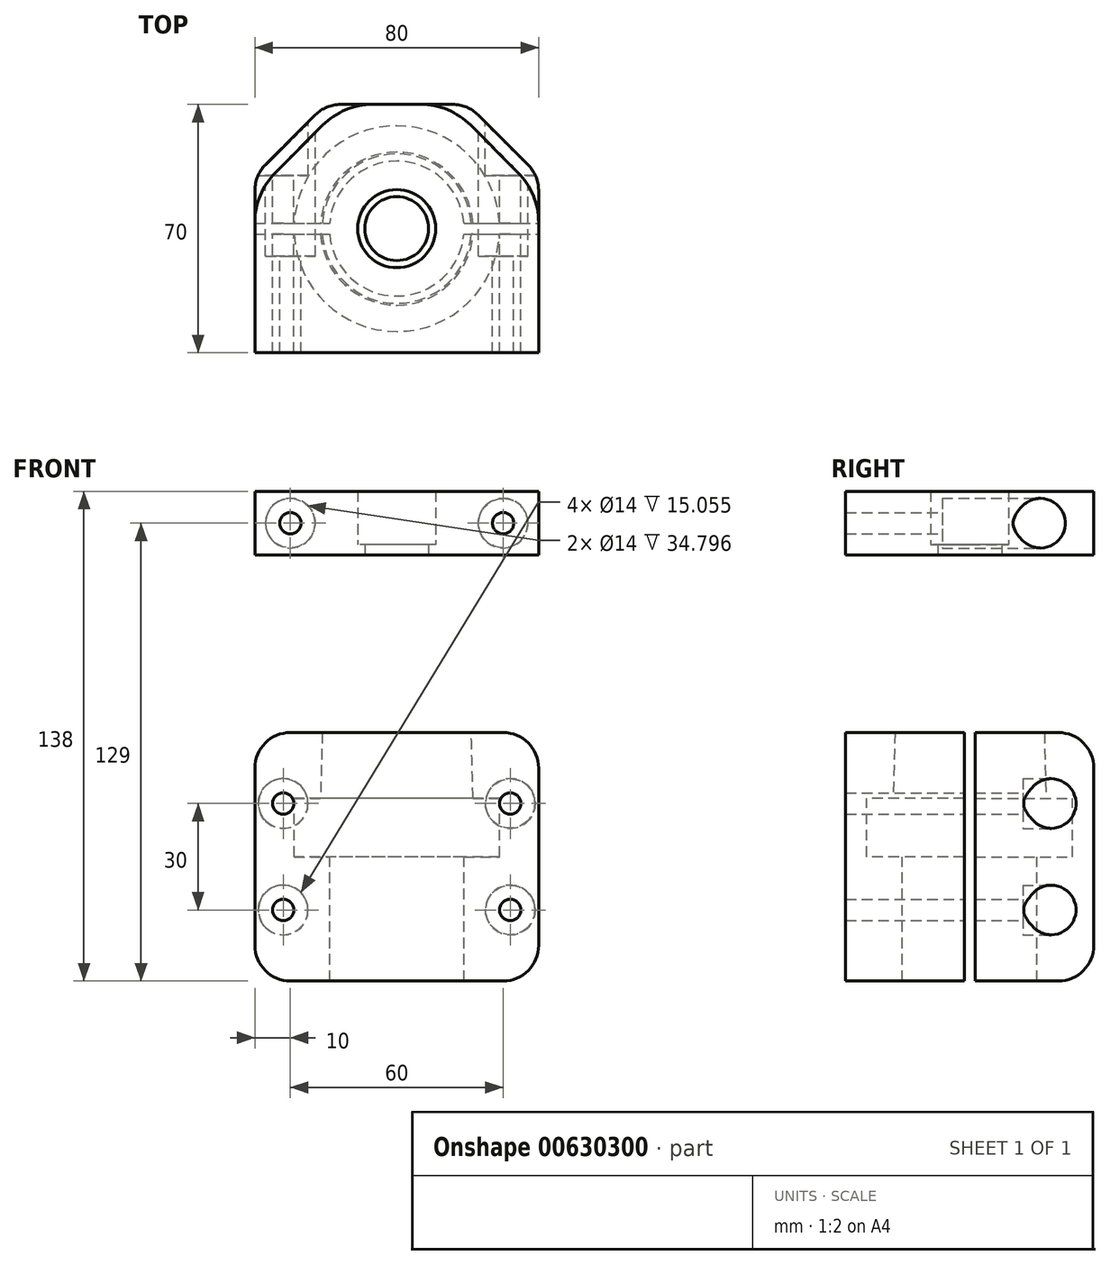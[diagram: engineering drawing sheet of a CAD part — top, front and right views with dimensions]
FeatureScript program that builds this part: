
annotation { "Feature Type Name" : "Feature", "Feature Type Description" : "" }
export const myFeature = defineFeature(function(context is Context, id is Id, definition is map)
    precondition{}
    {
        {
            var Q0;
            Q0=qCreatedBy(makeId("Front.planeOp"),FACE);
            var sketch = newSketch(context, id + "F0", { "sketchPlane" : qUnion([Q0])});
            skLineSegment(sketch, "E0", {"start": v(0, 86.22) * mm, "end": v(0, -59.94) * mm, "construction": true});
            skLineSegment(sketch, "E1.bottom", {"start": v(0, 0) * mm, "end": v(19, 0) * mm});
            skLineSegment(sketch, "E1.top", {"start": v(0, -38) * mm, "end": v(19, -38) * mm});
            skLineSegment(sketch, "E1.left", {"start": v(0, 0) * mm, "end": v(0, -38) * mm});
            skLineSegment(sketch, "E1.right", {"start": v(19, 0) * mm, "end": v(19, -38) * mm});
            skLineSegment(sketch, "E2", {"start": v(19, 0) * mm, "end": v(22, 0) * mm});
            skLineSegment(sketch, "E3", {"start": v(22, 0) * mm, "end": v(21, 36.99) * mm});
            skLineSegment(sketch, "E4", {"start": v(21, 36.99) * mm, "end": v(0, 36.99) * mm});
            skLineSegment(sketch, "E5", {"start": v(0, 36.99) * mm, "end": v(0, 0) * mm});
            skLineSegment(sketch, "E6.bottom", {"start": v(0, 0) * mm, "end": v(29, 0) * mm});
            skLineSegment(sketch, "E6.top", {"start": v(0, 16.5) * mm, "end": v(29, 16.5) * mm});
            skLineSegment(sketch, "E6.left", {"start": v(0, 0) * mm, "end": v(0, 16.5) * mm});
            skLineSegment(sketch, "E6.right", {"start": v(29, 0) * mm, "end": v(29, 16.5) * mm});
            skSolve(sketch);
        }
        {
            var Q0;
            Q0=makeQuery(id+"F0.imprint","IMPRINT",FACE,{"disambiguationData":[TD([[makeQuery(id+"F0.imprint","IMPRINT",EDGE,{"derivedFrom":sQuery(id+"F0.wireOp",EDGE,"E1.bottom")}),1.0]])]});
            var Q1;
            Q1=makeQuery(id+"F0.imprint","IMPRINT",FACE,{"disambiguationData":[TD([[makeQuery(id+"F0.imprint","IMPRINT",EDGE,{"derivedFrom":sQuery(id+"F0.wireOp",EDGE,"E1.bottom")}),-1.0]])]});
            var Q2;
            {var subQ3=sQuery(id+"F0.wireOp",EDGE,"E4");Q2=makeQuery(id+"F0.imprint","IMPRINT",FACE,{"disambiguationData":[TD([[makeQuery(id+"F0.imprint","IMPRINT",EDGE,{"derivedFrom":subQ3}),1.0]])]});}
            var Q3;
            {var subQ0=sQuery(id+"F0.wireOp",EDGE,"E6.bottom");Q3=makeQuery(id+"F0.imprint","IMPRINT",FACE,{"disambiguationData":[TD([[makeQuery(id+"F0.imprint","IMPRINT",EDGE,{"derivedFrom":subQ0}),1.0]])]});}
            var Q4;
            Q4=sQuery(id+"F0.wireOp",EDGE,"E0");
            revolve(context, id + "F1", {"surfaceOperationType" : NewSurfaceOperationType.NEW, "entities" : qUnion([Q0, Q1, Q2, Q3]), "axis" : qUnion([Q4]), "revolveType" : RevolveType.FULL});
        }
        {
            var Q0;
            Q0=qCreatedBy(makeId("Top.planeOp"),FACE);
            var sketch = newSketch(context, id + "F2", { "sketchPlane" : qUnion([Q0])});
            skLineSegment(sketch, "E7.bottom", {"start": v(-40, -35) * mm, "end": v(40, -35) * mm});
            skLineSegment(sketch, "E7.top", {"start": v(-40, 35) * mm, "end": v(40, 35) * mm});
            skLineSegment(sketch, "E7.left", {"start": v(-40, -35) * mm, "end": v(-40, 35) * mm});
            skLineSegment(sketch, "E7.right", {"start": v(40, -35) * mm, "end": v(40, 35) * mm});
            skPoint(sketch, "E7.middle", {"position": v(0, 0) * mm});
            skSolve(sketch);
        }
        {
            var Q0;
            Q0=makeQuery(id+"F2.imprint","IMPRINT",FACE,{"disambiguationData":[TD([[makeQuery(id+"F2.imprint","IMPRINT",EDGE,{"derivedFrom":sQuery(id+"F2.wireOp",EDGE,"E7.bottom")}),1.0]])]});
            extrude(context, id + "F3", {"entities" : qUnion([Q0]), "endBound" : BoundingType.SYMMETRIC, "depth" : 70 * mm, "offsetDistance" : 25 * mm});
        }
        {
            var Q0;
            Q0=makeQuery(id+"F1.opRevolve","SWEPT_BODY",BODY,{"disambiguationData":[OSD([sQuery(id+"F0.wireOp",EDGE,"E1.top"),sQuery(id+"F0.wireOp",EDGE,"E1.left"),sQuery(id+"F0.wireOp",EDGE,"E1.right"),sQuery(id+"F0.wireOp",EDGE,"E2"),sQuery(id+"F0.wireOp",EDGE,"E3"),sQuery(id+"F0.wireOp",EDGE,"E4"),sQuery(id+"F0.wireOp",EDGE,"E5")])]});
            var Q1;
            Q1=makeQuery(id+"F3.opExtrude","SWEPT_BODY",BODY,{"disambiguationData":[OSD([sQuery(id+"F2.wireOp",EDGE,"E7.bottom"),sQuery(id+"F2.wireOp",EDGE,"E7.top"),sQuery(id+"F2.wireOp",EDGE,"E7.left"),sQuery(id+"F2.wireOp",EDGE,"E7.right")])]});
            booleanBodies(context, id + "F4", {"operationType" : BooleanOperationType.SUBTRACTION, "tools" : qUnion([Q0]), "targets" : qUnion([Q1])});
        }
        {
            var Q0;
            Q0=makeQuery(id+"F3.opExtrude","CAP_FACE",FACE,{"disambiguationData":[OSD([sQuery(id+"F2.wireOp",EDGE,"E7.bottom"),sQuery(id+"F2.wireOp",EDGE,"E7.top"),sQuery(id+"F2.wireOp",EDGE,"E7.left"),sQuery(id+"F2.wireOp",EDGE,"E7.right")])],"isStart":true});
            var sketch = newSketch(context, id + "F5", { "sketchPlane" : qUnion([Q0])});
            skLineSegment(sketch, "E8.bottom", {"start": v(-40, 1.5) * mm, "end": v(40, 1.5) * mm});
            skLineSegment(sketch, "E8.top", {"start": v(-40, -1.5) * mm, "end": v(40, -1.5) * mm});
            skLineSegment(sketch, "E8.left", {"start": v(-40, 1.5) * mm, "end": v(-40, -1.5) * mm});
            skLineSegment(sketch, "E8.right", {"start": v(40, 1.5) * mm, "end": v(40, -1.5) * mm});
            skPoint(sketch, "E8.middle", {"position": v(0, 0) * mm});
            skSolve(sketch);
        }
        {
            var Q0;
            Q0 = qSketchRegion(id + "F5", true);
            extrude(context, id + "F6", {"entities" : qUnion([Q0]), "endBound" : BoundingType.SYMMETRIC, "depth" : 200 * mm, "offsetDistance" : 25 * mm});
        }
        {
            var Q0;
            Q0=makeQuery(id+"F6.opExtrude","SWEPT_BODY",BODY,{"disambiguationData":[OSD([sQuery(id+"F5.wireOp",EDGE,"E8.bottom"),sQuery(id+"F5.wireOp",EDGE,"E8.top"),sQuery(id+"F5.wireOp",EDGE,"E8.left"),sQuery(id+"F5.wireOp",EDGE,"E8.right")])]});
            var Q1;
            Q1=makeQuery(id+"F3.opExtrude","SWEPT_BODY",BODY,{"disambiguationData":[OSD([sQuery(id+"F2.wireOp",EDGE,"E7.bottom"),sQuery(id+"F2.wireOp",EDGE,"E7.top"),sQuery(id+"F2.wireOp",EDGE,"E7.left"),sQuery(id+"F2.wireOp",EDGE,"E7.right")])]});
            booleanBodies(context, id + "F7", {"operationType" : BooleanOperationType.SUBTRACTION, "tools" : qUnion([Q0]), "targets" : qUnion([Q1])});
        }
        {
            var Q0;
            Q0=makeQuery(id+"F3.opExtrude","SWEPT_FACE",FACE,{"disambiguationData":[OSD([sQuery(id+"F2.wireOp",EDGE,"E7.top")])]});
            var sketch = newSketch(context, id + "F8", { "sketchPlane" : qUnion([Q0])});
            skLineSegment(sketch, "E9", {"start": v(32, 0) * mm, "end": v(32, -15) * mm, "construction": true});
            skLineSegment(sketch, "E10", {"start": v(32, 0) * mm, "end": v(32, 15) * mm, "construction": true});
            skLineSegment(sketch, "E11", {"start": v(-32, 0) * mm, "end": v(-32, -15) * mm, "construction": true});
            skLineSegment(sketch, "E12", {"start": v(-32, 0) * mm, "end": v(-32, 15) * mm, "construction": true});
            skSolve(sketch);
        }
        {
            var Q0;
            Q0=sQuery(id+"F8.wireOp",VERTEX,"E9.end");
            var Q1;
            Q1=sQuery(id+"F8.wireOp",VERTEX,"E10.end");
            var Q2;
            Q2=sQuery(id+"F8.wireOp",VERTEX,"E12.end");
            var Q3;
            Q3=sQuery(id+"F8.wireOp",VERTEX,"E11.end");
            var Q4;
            Q4=makeQuery(id+"F7.opBoolean","SPLIT",BODY,{"disambiguationData":[OD(0.0)],"derivedFrom":makeQuery(id+"F3.opExtrude","SWEPT_BODY",BODY,{"disambiguationData":[OSD([sQuery(id+"F2.wireOp",EDGE,"E7.bottom"),sQuery(id+"F2.wireOp",EDGE,"E7.top"),sQuery(id+"F2.wireOp",EDGE,"E7.left"),sQuery(id+"F2.wireOp",EDGE,"E7.right")])]})});
            var Q5;
            Q5=makeQuery(id+"F7.opBoolean","SPLIT",BODY,{"disambiguationData":[OD(1.0)],"derivedFrom":makeQuery(id+"F3.opExtrude","SWEPT_BODY",BODY,{"disambiguationData":[OSD([sQuery(id+"F2.wireOp",EDGE,"E7.bottom"),sQuery(id+"F2.wireOp",EDGE,"E7.top"),sQuery(id+"F2.wireOp",EDGE,"E7.left"),sQuery(id+"F2.wireOp",EDGE,"E7.right")])]})});
            hole(context, id + "F9", {"style" : HoleStyle.C_BORE, "endStyle" : HoleEndStyle.THROUGH, "holeDiameter" : 6 * mm, "cBoreDiameter" : 14 * mm, "cBoreDepth" : 20 * mm, "majorDiameter" : 5 * mm, "isTappedThrough" : true, "tappedDepth" : 12 * mm, "tapClearance" : 3, "startFromSketch" : true, "locations" : qUnion([Q0, Q1, Q2, Q3]), "scope" : qUnion([Q4, Q5])});
        }
        {
            var Q0;
            Q0=makeQuery(id+"F3.opExtrude","SWEPT_EDGE",EDGE,{"disambiguationData":[OSD([sQuery(id+"F2.wireOp",EDGE,"E7.top"),sQuery(id+"F2.wireOp",EDGE,"E7.right")])]});
            var Q1;
            Q1=makeQuery(id+"F3.opExtrude","SWEPT_EDGE",EDGE,{"disambiguationData":[OSD([sQuery(id+"F2.wireOp",EDGE,"E7.top"),sQuery(id+"F2.wireOp",EDGE,"E7.left")])]});
            chamfer(context, id + "F10", {"entities" : qUnion([Q0, Q1]), "width" : 20 * mm, "tangentPropagation" : true});
        }
        {
            var Q0;
            {var subQ0=sQuery(id+"F2.wireOp",EDGE,"E7.bottom");var subQ1=sQuery(id+"F2.wireOp",EDGE,"E7.left");Q0=makeQuery(id+"F7.opBoolean","SPLIT",EDGE,{"disambiguationData":[TD([makeQuery(id+"F3.opExtrude","SWEPT_FACE",FACE,{"disambiguationData":[OSD([subQ0])]})])],"derivedFrom":makeQuery(id+"F3.opExtrude","CAP_EDGE",EDGE,{"disambiguationData":[OSD([subQ1])],"isStart":false})});}
            var Q1;
            {var subQ0=sQuery(id+"F2.wireOp",EDGE,"E7.left");var subQ1=sQuery(id+"F2.wireOp",EDGE,"E7.top");Q1=makeQuery(id+"F7.opBoolean","SPLIT",EDGE,{"disambiguationData":[TD([makeQuery(id+"F3.opExtrude","SWEPT_FACE",FACE,{"disambiguationData":[OSD([subQ1])]})])],"derivedFrom":makeQuery(id+"F3.opExtrude","CAP_EDGE",EDGE,{"disambiguationData":[OSD([subQ0])],"isStart":false})});}
            var Q2;
            {var subQ0=sQuery(id+"F2.wireOp",EDGE,"E7.right");var subQ1=sQuery(id+"F2.wireOp",EDGE,"E7.left");var subQ2=sQuery(id+"F2.wireOp",EDGE,"E7.top");Q2=makeQuery(id+"F10.opChamfer","BLEND_EDGE",EDGE,{"blendedFrom":[makeQuery(id+"F3.opExtrude","SWEPT_EDGE",EDGE,{"disambiguationData":[OSD([subQ2,subQ1])]}),makeQuery(id+"F7.opBoolean","SPLIT",FACE,{"disambiguationData":[TD([makeQuery(id+"F3.opExtrude","SWEPT_FACE",FACE,{"disambiguationData":[OSD([subQ2])]})])],"derivedFrom":makeQuery(id+"F3.opExtrude","CAP_FACE",FACE,{"disambiguationData":[OSD([sQuery(id+"F2.wireOp",EDGE,"E7.bottom"),subQ2,subQ1,subQ0])],"isStart":false})})],"blendedInto":[makeQuery(id+"F7.opBoolean","SPLIT",FACE,{"disambiguationData":[TD([makeQuery(id+"F3.opExtrude","SWEPT_FACE",FACE,{"disambiguationData":[OSD([subQ2])]})])],"derivedFrom":makeQuery(id+"F3.opExtrude","CAP_FACE",FACE,{"disambiguationData":[OSD([sQuery(id+"F2.wireOp",EDGE,"E7.bottom"),subQ2,subQ1,subQ0])],"isStart":false})})]});}
            var Q3;
            Q3=makeQuery(id+"F3.opExtrude","CAP_EDGE",EDGE,{"disambiguationData":[OSD([sQuery(id+"F2.wireOp",EDGE,"E7.top")])],"isStart":false});
            var Q4;
            {var subQ0=sQuery(id+"F2.wireOp",EDGE,"E7.right");var subQ1=sQuery(id+"F2.wireOp",EDGE,"E7.left");var subQ2=sQuery(id+"F2.wireOp",EDGE,"E7.top");Q4=makeQuery(id+"F10.opChamfer","BLEND_EDGE",EDGE,{"blendedFrom":[makeQuery(id+"F3.opExtrude","SWEPT_EDGE",EDGE,{"disambiguationData":[OSD([subQ2,subQ0])]}),makeQuery(id+"F7.opBoolean","SPLIT",FACE,{"disambiguationData":[TD([makeQuery(id+"F3.opExtrude","SWEPT_FACE",FACE,{"disambiguationData":[OSD([subQ2])]})])],"derivedFrom":makeQuery(id+"F3.opExtrude","CAP_FACE",FACE,{"disambiguationData":[OSD([sQuery(id+"F2.wireOp",EDGE,"E7.bottom"),subQ2,subQ1,subQ0])],"isStart":false})})],"blendedInto":[makeQuery(id+"F7.opBoolean","SPLIT",FACE,{"disambiguationData":[TD([makeQuery(id+"F3.opExtrude","SWEPT_FACE",FACE,{"disambiguationData":[OSD([subQ2])]})])],"derivedFrom":makeQuery(id+"F3.opExtrude","CAP_FACE",FACE,{"disambiguationData":[OSD([sQuery(id+"F2.wireOp",EDGE,"E7.bottom"),subQ2,subQ1,subQ0])],"isStart":false})})]});}
            var Q5;
            {var subQ0=sQuery(id+"F2.wireOp",EDGE,"E7.right");var subQ1=sQuery(id+"F2.wireOp",EDGE,"E7.top");Q5=makeQuery(id+"F7.opBoolean","SPLIT",EDGE,{"disambiguationData":[TD([makeQuery(id+"F3.opExtrude","SWEPT_FACE",FACE,{"disambiguationData":[OSD([subQ1])]})])],"derivedFrom":makeQuery(id+"F3.opExtrude","CAP_EDGE",EDGE,{"disambiguationData":[OSD([subQ0])],"isStart":false})});}
            var Q6;
            {var subQ0=sQuery(id+"F2.wireOp",EDGE,"E7.bottom");var subQ1=sQuery(id+"F2.wireOp",EDGE,"E7.right");Q6=makeQuery(id+"F7.opBoolean","SPLIT",EDGE,{"disambiguationData":[TD([makeQuery(id+"F3.opExtrude","SWEPT_FACE",FACE,{"disambiguationData":[OSD([subQ0])]})])],"derivedFrom":makeQuery(id+"F3.opExtrude","CAP_EDGE",EDGE,{"disambiguationData":[OSD([subQ1])],"isStart":false})});}
            var Q7;
            {var subQ0=sQuery(id+"F2.wireOp",EDGE,"E7.bottom");var subQ1=sQuery(id+"F2.wireOp",EDGE,"E7.right");Q7=makeQuery(id+"F7.opBoolean","SPLIT",EDGE,{"disambiguationData":[TD([makeQuery(id+"F3.opExtrude","SWEPT_FACE",FACE,{"disambiguationData":[OSD([subQ0])]})])],"derivedFrom":makeQuery(id+"F3.opExtrude","CAP_EDGE",EDGE,{"disambiguationData":[OSD([subQ1])],"isStart":true})});}
            var Q8;
            {var subQ0=sQuery(id+"F2.wireOp",EDGE,"E7.right");var subQ1=sQuery(id+"F2.wireOp",EDGE,"E7.top");Q8=makeQuery(id+"F7.opBoolean","SPLIT",EDGE,{"disambiguationData":[TD([makeQuery(id+"F3.opExtrude","SWEPT_FACE",FACE,{"disambiguationData":[OSD([subQ1])]})])],"derivedFrom":makeQuery(id+"F3.opExtrude","CAP_EDGE",EDGE,{"disambiguationData":[OSD([subQ0])],"isStart":true})});}
            var Q9;
            {var subQ0=sQuery(id+"F2.wireOp",EDGE,"E7.left");var subQ1=sQuery(id+"F2.wireOp",EDGE,"E7.right");var subQ2=sQuery(id+"F2.wireOp",EDGE,"E7.top");Q9=makeQuery(id+"F10.opChamfer","BLEND_EDGE",EDGE,{"blendedFrom":[makeQuery(id+"F3.opExtrude","SWEPT_EDGE",EDGE,{"disambiguationData":[OSD([subQ2,subQ1])]}),makeQuery(id+"F7.opBoolean","SPLIT",FACE,{"disambiguationData":[TD([makeQuery(id+"F3.opExtrude","SWEPT_FACE",FACE,{"disambiguationData":[OSD([subQ2])]})])],"derivedFrom":makeQuery(id+"F3.opExtrude","CAP_FACE",FACE,{"disambiguationData":[OSD([sQuery(id+"F2.wireOp",EDGE,"E7.bottom"),subQ2,subQ0,subQ1])],"isStart":true})})],"blendedInto":[makeQuery(id+"F7.opBoolean","SPLIT",FACE,{"disambiguationData":[TD([makeQuery(id+"F3.opExtrude","SWEPT_FACE",FACE,{"disambiguationData":[OSD([subQ2])]})])],"derivedFrom":makeQuery(id+"F3.opExtrude","CAP_FACE",FACE,{"disambiguationData":[OSD([sQuery(id+"F2.wireOp",EDGE,"E7.bottom"),subQ2,subQ0,subQ1])],"isStart":true})})]});}
            var Q10;
            Q10=makeQuery(id+"F3.opExtrude","CAP_EDGE",EDGE,{"disambiguationData":[OSD([sQuery(id+"F2.wireOp",EDGE,"E7.top")])],"isStart":true});
            var Q11;
            {var subQ0=sQuery(id+"F2.wireOp",EDGE,"E7.left");var subQ1=sQuery(id+"F2.wireOp",EDGE,"E7.right");var subQ2=sQuery(id+"F2.wireOp",EDGE,"E7.top");Q11=makeQuery(id+"F10.opChamfer","BLEND_EDGE",EDGE,{"blendedFrom":[makeQuery(id+"F3.opExtrude","SWEPT_EDGE",EDGE,{"disambiguationData":[OSD([subQ2,subQ0])]}),makeQuery(id+"F7.opBoolean","SPLIT",FACE,{"disambiguationData":[TD([makeQuery(id+"F3.opExtrude","SWEPT_FACE",FACE,{"disambiguationData":[OSD([subQ2])]})])],"derivedFrom":makeQuery(id+"F3.opExtrude","CAP_FACE",FACE,{"disambiguationData":[OSD([sQuery(id+"F2.wireOp",EDGE,"E7.bottom"),subQ2,subQ0,subQ1])],"isStart":true})})],"blendedInto":[makeQuery(id+"F7.opBoolean","SPLIT",FACE,{"disambiguationData":[TD([makeQuery(id+"F3.opExtrude","SWEPT_FACE",FACE,{"disambiguationData":[OSD([subQ2])]})])],"derivedFrom":makeQuery(id+"F3.opExtrude","CAP_FACE",FACE,{"disambiguationData":[OSD([sQuery(id+"F2.wireOp",EDGE,"E7.bottom"),subQ2,subQ0,subQ1])],"isStart":true})})]});}
            var Q12;
            {var subQ0=sQuery(id+"F2.wireOp",EDGE,"E7.left");var subQ1=sQuery(id+"F2.wireOp",EDGE,"E7.top");Q12=makeQuery(id+"F7.opBoolean","SPLIT",EDGE,{"disambiguationData":[TD([makeQuery(id+"F3.opExtrude","SWEPT_FACE",FACE,{"disambiguationData":[OSD([subQ1])]})])],"derivedFrom":makeQuery(id+"F3.opExtrude","CAP_EDGE",EDGE,{"disambiguationData":[OSD([subQ0])],"isStart":true})});}
            var Q13;
            {var subQ0=sQuery(id+"F2.wireOp",EDGE,"E7.bottom");var subQ1=sQuery(id+"F2.wireOp",EDGE,"E7.left");Q13=makeQuery(id+"F7.opBoolean","SPLIT",EDGE,{"disambiguationData":[TD([makeQuery(id+"F3.opExtrude","SWEPT_FACE",FACE,{"disambiguationData":[OSD([subQ0])]})])],"derivedFrom":makeQuery(id+"F3.opExtrude","CAP_EDGE",EDGE,{"disambiguationData":[OSD([subQ1])],"isStart":true})});}
            var Q14;
            {var subQ0=sQuery(id+"F2.wireOp",EDGE,"E7.right");var subQ2=sQuery(id+"F2.wireOp",EDGE,"E7.top");Q14=makeQuery(id+"F10.opChamfer","BLEND_EDGE",EDGE,{"blendedFrom":[makeQuery(id+"F3.opExtrude","SWEPT_EDGE",EDGE,{"disambiguationData":[OSD([subQ2,subQ0])]}),makeQuery(id+"F7.opBoolean","SPLIT",FACE,{"disambiguationData":[TD([makeQuery(id+"F3.opExtrude","SWEPT_FACE",FACE,{"disambiguationData":[OSD([subQ2])]})])],"derivedFrom":makeQuery(id+"F3.opExtrude","SWEPT_FACE",FACE,{"disambiguationData":[OSD([subQ0])]})})],"blendedInto":[makeQuery(id+"F7.opBoolean","SPLIT",FACE,{"disambiguationData":[TD([makeQuery(id+"F3.opExtrude","SWEPT_FACE",FACE,{"disambiguationData":[OSD([subQ2])]})])],"derivedFrom":makeQuery(id+"F3.opExtrude","SWEPT_FACE",FACE,{"disambiguationData":[OSD([subQ0])]})})]});}
            var Q15;
            {var subQ0=sQuery(id+"F2.wireOp",EDGE,"E7.top");Q15=makeQuery(id+"F10.opChamfer","BLEND_EDGE",EDGE,{"blendedFrom":[makeQuery(id+"F3.opExtrude","SWEPT_EDGE",EDGE,{"disambiguationData":[OSD([subQ0,sQuery(id+"F2.wireOp",EDGE,"E7.right")])]}),makeQuery(id+"F3.opExtrude","SWEPT_FACE",FACE,{"disambiguationData":[OSD([subQ0])]})],"blendedInto":[makeQuery(id+"F3.opExtrude","SWEPT_FACE",FACE,{"disambiguationData":[OSD([subQ0])]})]});}
            var Q16;
            {var subQ0=sQuery(id+"F2.wireOp",EDGE,"E7.top");Q16=makeQuery(id+"F10.opChamfer","BLEND_EDGE",EDGE,{"blendedFrom":[makeQuery(id+"F3.opExtrude","SWEPT_EDGE",EDGE,{"disambiguationData":[OSD([subQ0,sQuery(id+"F2.wireOp",EDGE,"E7.left")])]}),makeQuery(id+"F3.opExtrude","SWEPT_FACE",FACE,{"disambiguationData":[OSD([subQ0])]})],"blendedInto":[makeQuery(id+"F3.opExtrude","SWEPT_FACE",FACE,{"disambiguationData":[OSD([subQ0])]})]});}
            var Q17;
            {var subQ1=sQuery(id+"F2.wireOp",EDGE,"E7.left");var subQ2=sQuery(id+"F2.wireOp",EDGE,"E7.top");Q17=makeQuery(id+"F10.opChamfer","BLEND_EDGE",EDGE,{"blendedFrom":[makeQuery(id+"F3.opExtrude","SWEPT_EDGE",EDGE,{"disambiguationData":[OSD([subQ2,subQ1])]}),makeQuery(id+"F7.opBoolean","SPLIT",FACE,{"disambiguationData":[TD([makeQuery(id+"F3.opExtrude","SWEPT_FACE",FACE,{"disambiguationData":[OSD([subQ2])]})])],"derivedFrom":makeQuery(id+"F3.opExtrude","SWEPT_FACE",FACE,{"disambiguationData":[OSD([subQ1])]})})],"blendedInto":[makeQuery(id+"F7.opBoolean","SPLIT",FACE,{"disambiguationData":[TD([makeQuery(id+"F3.opExtrude","SWEPT_FACE",FACE,{"disambiguationData":[OSD([subQ2])]})])],"derivedFrom":makeQuery(id+"F3.opExtrude","SWEPT_FACE",FACE,{"disambiguationData":[OSD([subQ1])]})})]});}
            fillet(context, id + "F11", {"entities" : qUnion([Q0, Q1, Q2, Q3, Q4, Q5, Q6, Q7, Q8, Q9, Q10, Q11, Q12, Q13, Q14, Q15, Q16, Q17]), "tangentPropagation" : true, "radius" : 10 * mm, "defaultsChanged" : true, "vertexSettings" : [], "allowEdgeOverflow" : false});
        }
        {
            var Q0;
            {var subQ0=sQuery(id+"F2.wireOp",EDGE,"E7.left");var subQ1=sQuery(id+"F2.wireOp",EDGE,"E7.right");var subQ2=sQuery(id+"F2.wireOp",EDGE,"E7.bottom");Q0=makeQuery(id+"F7.opBoolean","SPLIT",FACE,{"disambiguationData":[TD([makeQuery(id+"F3.opExtrude","SWEPT_FACE",FACE,{"disambiguationData":[OSD([subQ2])]})])],"derivedFrom":makeQuery(id+"F3.opExtrude","CAP_FACE",FACE,{"disambiguationData":[OSD([subQ2,sQuery(id+"F2.wireOp",EDGE,"E7.top"),subQ0,subQ1])],"isStart":false})});}
            cPlane(context, id + "F12", {"entities" : qUnion([Q0]), "cplaneType" : CPlaneType.OFFSET, "offset" : 50 * mm, "width" : 150 * mm, "height" : 150 * mm});
        }
        {
            var Q0;
            Q0=qCreatedBy(id+"F12.planeOp",FACE);
            var sketch = newSketch(context, id + "F13", { "sketchPlane" : qUnion([Q0])});
            skPoint(sketch, "E13.0", {"position": v(0, 0) * mm});
            skLineSegment(sketch, "E14.0", {"start": v(-30, -35) * mm, "end": v(30, -35) * mm});
            skLineSegment(sketch, "E15.0", {"start": v(-15.86, 35) * mm, "end": v(15.86, 35) * mm});
            skLineSegment(sketch, "E16.0", {"start": v(-40, -35) * mm, "end": v(-40, -1.5) * mm});
            skLineSegment(sketch, "E17.0", {"start": v(40, -1.5) * mm, "end": v(40, -35) * mm});
            skLineSegment(sketch, "E18", {"start": v(40, -35) * mm, "end": v(30, -35) * mm});
            skLineSegment(sketch, "E19", {"start": v(-30, -35) * mm, "end": v(-40, -35) * mm});
            skCircle(sketch, "E20", {"center": v(0, 0) * mm, "radius": 9 * mm});
            skCircle(sketch, "E21", {"center": v(0, 0) * mm, "radius": 11 * mm});
            skLineSegment(sketch, "E22", {"start": v(40, -1.5) * mm, "end": v(40, 35) * mm});
            skLineSegment(sketch, "E23", {"start": v(40, 35) * mm, "end": v(15.86, 35) * mm});
            skLineSegment(sketch, "E24", {"start": v(-40, -1.5) * mm, "end": v(-40, 35) * mm});
            skLineSegment(sketch, "E25", {"start": v(-40, 35) * mm, "end": v(-15.86, 35) * mm});
            skSolve(sketch);
        }
        {
            var Q0;
            Q0=makeQuery(id+"F13.imprint","IMPRINT",FACE,{"disambiguationData":[TD([[makeQuery(id+"F13.imprint","IMPRINT",EDGE,{"derivedFrom":sQuery(id+"F13.wireOp",EDGE,"E14.0")}),1.0]])]});
            extrude(context, id + "F14", {"entities" : qUnion([Q0]), "depth" : 18 * mm, "offsetDistance" : 25 * mm});
        }
        {
            var Q0;
            Q0=makeQuery(id+"F14.opExtrude","SWEPT_FACE",FACE,{"disambiguationData":[OSD([sQuery(id+"F13.wireOp",EDGE,"E15.0"),sQuery(id+"F13.wireOp",EDGE,"E23"),sQuery(id+"F13.wireOp",EDGE,"E25")])]});
            var sketch = newSketch(context, id + "F15", { "sketchPlane" : qUnion([Q0])});
            skLineSegment(sketch, "E26", {"start": v(40, 94) * mm, "end": v(30, 94) * mm, "construction": true});
            skLineSegment(sketch, "E27", {"start": v(-40, 94) * mm, "end": v(-30, 94) * mm, "construction": true});
            skSolve(sketch);
        }
        {
            var Q0;
            Q0=makeQuery(id+"F13.imprint","IMPRINT",FACE,{"disambiguationData":[TD([[makeQuery(id+"F13.imprint","IMPRINT",EDGE,{"derivedFrom":sQuery(id+"F13.wireOp",EDGE,"E20")}),-1.0]])]});
            extrude(context, id + "F16", {"entities" : qUnion([Q0]), "operationType" : NewBodyOperationType.ADD, "depth" : 3 * mm, "offsetDistance" : 25 * mm});
        }
        {
            var Q0;
            Q0=makeQuery(id+"F14.opExtrude","SWEPT_EDGE",EDGE,{"disambiguationData":[OSD([sQuery(id+"F13.wireOp",EDGE,"E22"),sQuery(id+"F13.wireOp",EDGE,"E23")])]});
            var Q1;
            Q1=makeQuery(id+"F14.opExtrude","SWEPT_EDGE",EDGE,{"disambiguationData":[OSD([sQuery(id+"F13.wireOp",EDGE,"E24"),sQuery(id+"F13.wireOp",EDGE,"E25")])]});
            chamfer(context, id + "F17", {"entities" : qUnion([Q0, Q1]), "width" : 25 * mm, "tangentPropagation" : true});
        }
        {
            var Q0;
            {var subQ0=sQuery(id+"F13.wireOp",EDGE,"E23");Q0=makeQuery(id+"F17.opChamfer","BLEND_EDGE",EDGE,{"blendedFrom":[makeQuery(id+"F14.opExtrude","SWEPT_EDGE",EDGE,{"disambiguationData":[OSD([sQuery(id+"F13.wireOp",EDGE,"E22"),subQ0])]}),makeQuery(id+"F14.opExtrude","SWEPT_FACE",FACE,{"disambiguationData":[OSD([sQuery(id+"F13.wireOp",EDGE,"E15.0"),subQ0,sQuery(id+"F13.wireOp",EDGE,"E25")])]})],"blendedInto":[makeQuery(id+"F14.opExtrude","SWEPT_FACE",FACE,{"disambiguationData":[OSD([sQuery(id+"F13.wireOp",EDGE,"E15.0"),subQ0,sQuery(id+"F13.wireOp",EDGE,"E25")])]})]});}
            var Q1;
            {var subQ0=sQuery(id+"F13.wireOp",EDGE,"E22");Q1=makeQuery(id+"F17.opChamfer","BLEND_EDGE",EDGE,{"blendedFrom":[makeQuery(id+"F14.opExtrude","SWEPT_EDGE",EDGE,{"disambiguationData":[OSD([subQ0,sQuery(id+"F13.wireOp",EDGE,"E23")])]}),makeQuery(id+"F14.opExtrude","SWEPT_FACE",FACE,{"disambiguationData":[OSD([sQuery(id+"F13.wireOp",EDGE,"E17.0"),subQ0])]})],"blendedInto":[makeQuery(id+"F14.opExtrude","SWEPT_FACE",FACE,{"disambiguationData":[OSD([sQuery(id+"F13.wireOp",EDGE,"E17.0"),subQ0])]})]});}
            var Q2;
            {var subQ0=sQuery(id+"F13.wireOp",EDGE,"E25");Q2=makeQuery(id+"F17.opChamfer","BLEND_EDGE",EDGE,{"blendedFrom":[makeQuery(id+"F14.opExtrude","SWEPT_EDGE",EDGE,{"disambiguationData":[OSD([sQuery(id+"F13.wireOp",EDGE,"E24"),subQ0])]}),makeQuery(id+"F14.opExtrude","SWEPT_FACE",FACE,{"disambiguationData":[OSD([sQuery(id+"F13.wireOp",EDGE,"E15.0"),sQuery(id+"F13.wireOp",EDGE,"E23"),subQ0])]})],"blendedInto":[makeQuery(id+"F14.opExtrude","SWEPT_FACE",FACE,{"disambiguationData":[OSD([sQuery(id+"F13.wireOp",EDGE,"E15.0"),sQuery(id+"F13.wireOp",EDGE,"E23"),subQ0])]})]});}
            var Q3;
            {var subQ0=sQuery(id+"F13.wireOp",EDGE,"E24");Q3=makeQuery(id+"F17.opChamfer","BLEND_EDGE",EDGE,{"blendedFrom":[makeQuery(id+"F14.opExtrude","SWEPT_EDGE",EDGE,{"disambiguationData":[OSD([subQ0,sQuery(id+"F13.wireOp",EDGE,"E25")])]}),makeQuery(id+"F14.opExtrude","SWEPT_FACE",FACE,{"disambiguationData":[OSD([sQuery(id+"F13.wireOp",EDGE,"E16.0"),subQ0])]})],"blendedInto":[makeQuery(id+"F14.opExtrude","SWEPT_FACE",FACE,{"disambiguationData":[OSD([sQuery(id+"F13.wireOp",EDGE,"E16.0"),subQ0])]})]});}
            fillet(context, id + "F18", {"entities" : qUnion([Q0, Q1, Q2, Q3]), "tangentPropagation" : true, "radius" : 20 * mm, "defaultsChanged" : true, "vertexSettings" : [], "allowEdgeOverflow" : false});
        }
        {
            var Q0;
            Q0=sQuery(id+"F15.wireOp",VERTEX,"E26.end");
            var Q1;
            Q1=sQuery(id+"F15.wireOp",VERTEX,"E27.end");
            var Q2;
            Q2=makeQuery(id+"F14.opExtrude","SWEPT_BODY",BODY,{"disambiguationData":[OSD([sQuery(id+"F13.wireOp",EDGE,"E14.0"),sQuery(id+"F13.wireOp",EDGE,"E15.0"),sQuery(id+"F13.wireOp",EDGE,"E16.0"),sQuery(id+"F13.wireOp",EDGE,"E17.0"),sQuery(id+"F13.wireOp",EDGE,"E18"),sQuery(id+"F13.wireOp",EDGE,"E19"),sQuery(id+"F13.wireOp",EDGE,"E21"),sQuery(id+"F13.wireOp",EDGE,"E22"),sQuery(id+"F13.wireOp",EDGE,"E23"),sQuery(id+"F13.wireOp",EDGE,"E24"),sQuery(id+"F13.wireOp",EDGE,"E25")])]});
            hole(context, id + "F19", {"style" : HoleStyle.C_BORE, "endStyle" : HoleEndStyle.THROUGH, "holeDiameter" : 6 * mm, "cBoreDiameter" : 14 * mm, "cBoreDepth" : 20 * mm, "majorDiameter" : 5 * mm, "isTappedThrough" : true, "tappedDepth" : 12 * mm, "tapClearance" : 3, "locations" : qUnion([Q0, Q1]), "scope" : qUnion([Q2])});
        }
    });
